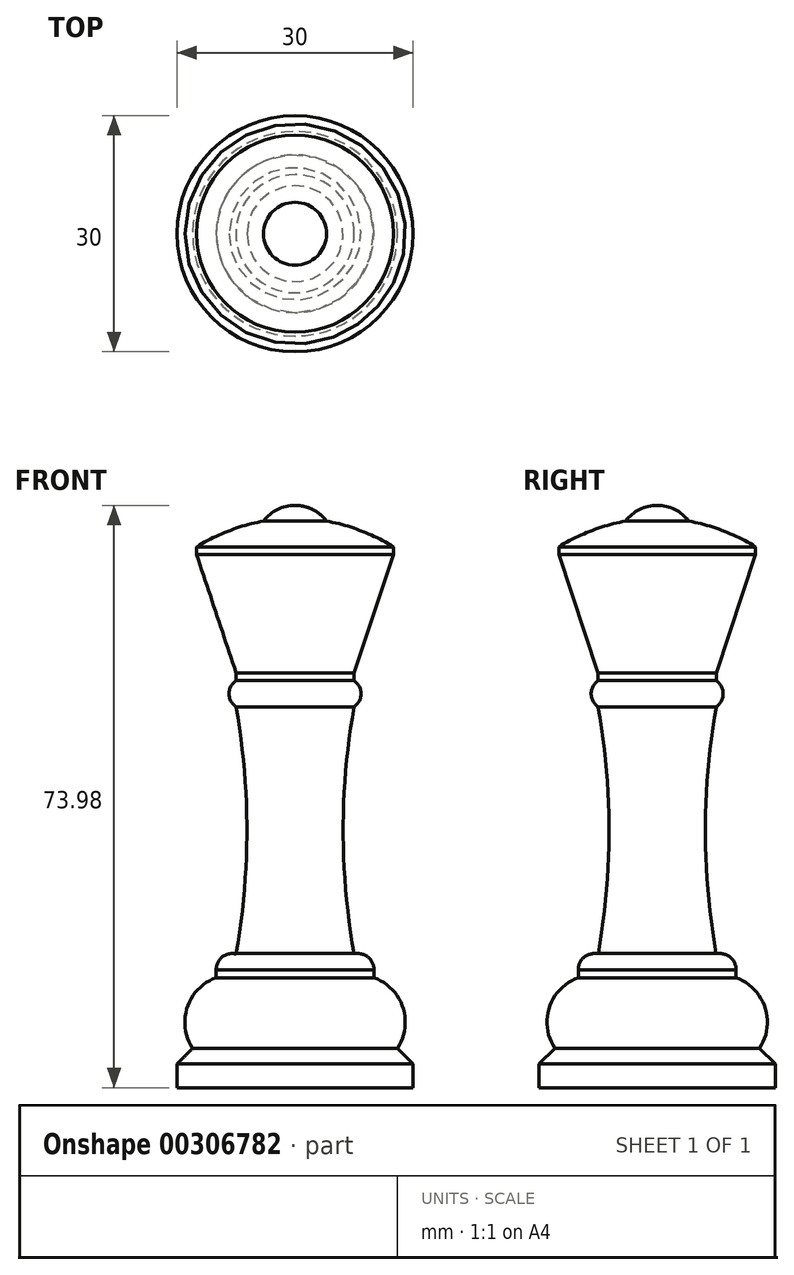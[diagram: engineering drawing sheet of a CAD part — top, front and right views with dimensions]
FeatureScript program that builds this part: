
annotation { "Feature Type Name" : "Feature", "Feature Type Description" : "" }
export const myFeature = defineFeature(function(context is Context, id is Id, definition is map)
    precondition{}
    {
        {
            var Q0;
            Q0=qCreatedBy(makeId("Front.planeOp"),FACE);
            var sketch = newSketch(context, id + "F0", { "sketchPlane" : qUnion([Q0])});
            skArc(sketch, "E0", {"start": v(4, -2) * mm, "mid": v(2.24, -0.53) * mm, "end": v(0, 0) * mm});
            skArc(sketch, "E1", {"start": v(12.5, -5.27) * mm, "mid": v(8.4, -3.24) * mm, "end": v(4, -2) * mm});
            skLineSegment(sketch, "E2", {"start": v(12.5, -5.27) * mm, "end": v(12.5, -6.27) * mm});
            skLineSegment(sketch, "E3", {"start": v(12.5, -6.27) * mm, "end": v(7.5, -21.27) * mm});
            skLineSegment(sketch, "E4", {"start": v(7.5, -21.27) * mm, "end": v(7.5, -22.27) * mm});
            skArc(sketch, "E5", {"start": v(7.5, -25.6) * mm, "mid": v(8.38, -23.93) * mm, "end": v(7.5, -22.27) * mm});
            skArc(sketch, "E6", {"start": v(7.5, -25.6) * mm, "mid": v(6.12, -41.3) * mm, "end": v(7.5, -57) * mm});
            skArc(sketch, "E7", {"start": v(10, -59) * mm, "mid": v(9.26, -57.38) * mm, "end": v(7.5, -57) * mm});
            skLineSegment(sketch, "E8", {"start": v(10, -59) * mm, "end": v(10, -60) * mm});
            skArc(sketch, "E9", {"start": v(13, -68.98) * mm, "mid": v(13.7, -63.76) * mm, "end": v(10, -60) * mm});
            skLineSegment(sketch, "E10", {"start": v(15, -70.98) * mm, "end": v(13, -68.98) * mm});
            skLineSegment(sketch, "E11", {"start": v(15, -70.98) * mm, "end": v(15, -73.98) * mm});
            skLineSegment(sketch, "E12", {"start": v(15, -73.98) * mm, "end": v(0, -73.98) * mm});
            skLineSegment(sketch, "E13", {"start": v(0, -73.98) * mm, "end": v(0, 0) * mm});
            skSolve(sketch);
        }
        {
            var Q0;
            Q0=makeQuery(id+"F0.imprint","IMPRINT",FACE,{"disambiguationData":[TD([[makeQuery(id+"F0.imprint","IMPRINT",EDGE,{"derivedFrom":sQuery(id+"F0.wireOp",EDGE,"E0")}),1.0]])]});
            var Q1;
            Q1=sQuery(id+"F0.wireOp",EDGE,"E13");
            revolve(context, id + "F1", {"entities" : qUnion([Q0]), "axis" : qUnion([Q1]), "revolveType" : RevolveType.FULL});
        }
    });
